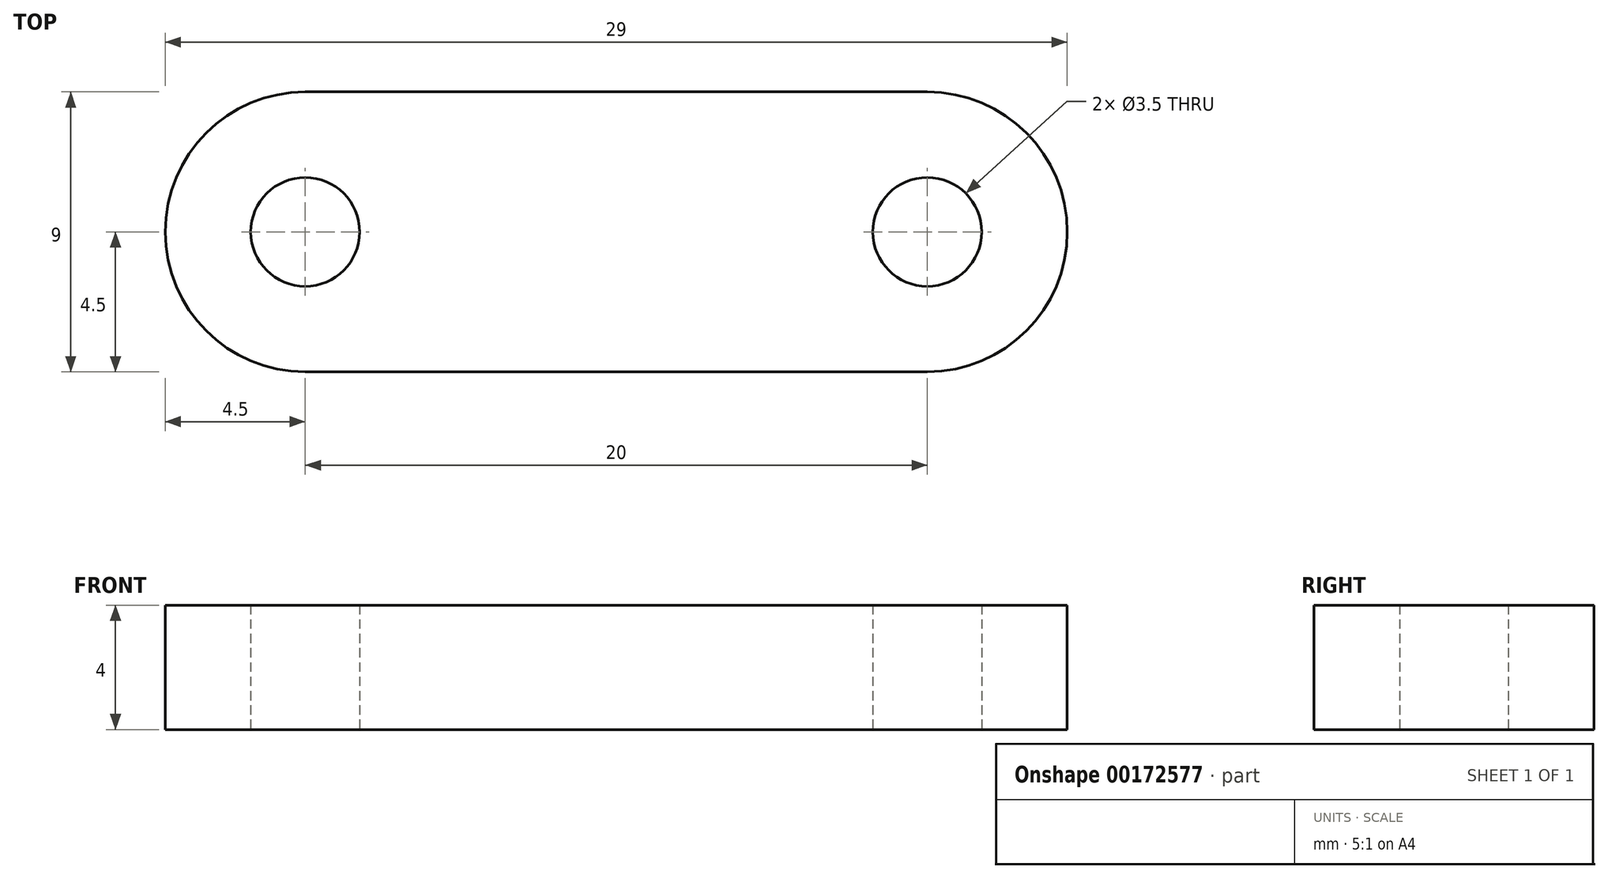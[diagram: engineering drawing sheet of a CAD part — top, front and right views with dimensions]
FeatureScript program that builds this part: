
annotation { "Feature Type Name" : "Feature", "Feature Type Description" : "" }
export const myFeature = defineFeature(function(context is Context, id is Id, definition is map)
    precondition{}
    {
        {
            var Q0;
            Q0=qCreatedBy(makeId("Top.planeOp"),FACE);
            var sketch = newSketch(context, id + "F0", { "sketchPlane" : qUnion([Q0])});
            skCircle(sketch, "E0", {"center": v(0, 0) * mm, "radius": 4.5 * mm});
            skCircle(sketch, "E1", {"center": v(20, 0) * mm, "radius": 4.5 * mm});
            skLineSegment(sketch, "E2.bottom", {"start": v(0, 4.5) * mm, "end": v(20, 4.5) * mm});
            skLineSegment(sketch, "E2.top", {"start": v(0, -4.5) * mm, "end": v(20, -4.5) * mm});
            skLineSegment(sketch, "E2.left", {"start": v(0, 4.5) * mm, "end": v(0, -4.5) * mm});
            skLineSegment(sketch, "E2.right", {"start": v(20, 4.5) * mm, "end": v(20, -4.5) * mm});
            skCircle(sketch, "E3", {"center": v(0, 0) * mm, "radius": 1.75 * mm});
            skCircle(sketch, "E4", {"center": v(20, 0) * mm, "radius": 1.75 * mm});
            skSolve(sketch);
        }
        {
            var Q0;
            Q0 = qSketchRegion(id + "F0", true);
            extrude(context, id + "F1", {"entities" : qUnion([Q0]), "depth" : 4 * mm, "offsetDistance" : 25 * mm});
        }
    });
